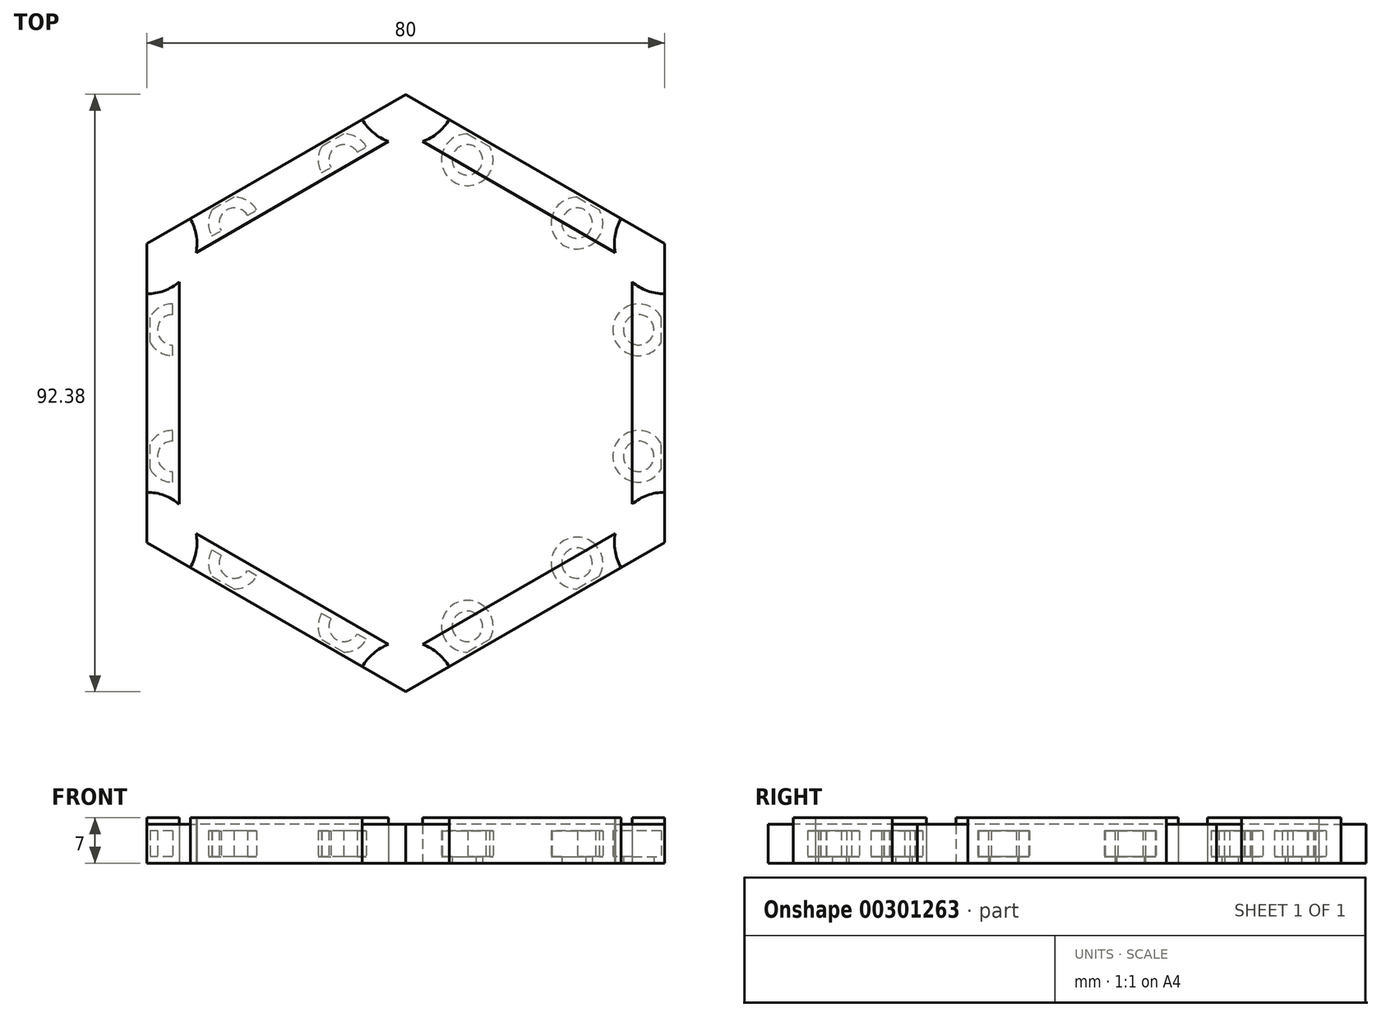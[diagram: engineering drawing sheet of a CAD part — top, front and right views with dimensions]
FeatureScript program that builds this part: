
annotation { "Feature Type Name" : "Feature", "Feature Type Description" : "" }
export const myFeature = defineFeature(function(context is Context, id is Id, definition is map)
    precondition{}
    {
        {
            var Q0;
            Q0=qCreatedBy(makeId("Top.planeOp"),FACE);
            var sketch = newSketch(context, id + "F0", { "sketchPlane" : qUnion([Q0])});
            skCircle(sketch, "E0.cCircle", {"center": v(0, 0) * mm, "radius": 40 * mm, "construction": true});
            skLineSegment(sketch, "E0.0", {"start": v(40, 23.1) * mm, "end": v(40, -23.1) * mm});
            skLineSegment(sketch, "E0.1", {"start": v(40, -23.1) * mm, "end": v(0, -46.19) * mm});
            skLineSegment(sketch, "E0.2", {"start": v(0, -46.19) * mm, "end": v(-40, -23.1) * mm});
            skLineSegment(sketch, "E0.3", {"start": v(-40, -23.1) * mm, "end": v(-40, 23.1) * mm});
            skLineSegment(sketch, "E0.4", {"start": v(-40, 23.1) * mm, "end": v(0, 46.19) * mm});
            skLineSegment(sketch, "E0.5", {"start": v(0, 46.19) * mm, "end": v(40, 23.1) * mm});
            skPoint(sketch, "E0.0.midPoint", {"position": v(40, 0) * mm});
            skCircle(sketch, "E1.cCircle", {"center": v(0, 0) * mm, "radius": 35 * mm, "construction": true});
            skLineSegment(sketch, "E1.0", {"start": v(35, 20.2) * mm, "end": v(35, -20.2) * mm});
            skLineSegment(sketch, "E1.1", {"start": v(35, -20.2) * mm, "end": v(0, -40.41) * mm});
            skLineSegment(sketch, "E1.2", {"start": v(0, -40.41) * mm, "end": v(-35, -20.2) * mm});
            skLineSegment(sketch, "E1.3", {"start": v(-35, -20.2) * mm, "end": v(-35, 20.2) * mm});
            skLineSegment(sketch, "E1.4", {"start": v(-35, 20.2) * mm, "end": v(0, 40.41) * mm});
            skLineSegment(sketch, "E1.5", {"start": v(0, 40.41) * mm, "end": v(35, 20.2) * mm});
            skPoint(sketch, "E1.0.midPoint", {"position": v(35, 0) * mm});
            skArc(sketch, "E2", {"start": v(-40, 15.34) * mm, "mid": v(-33.29, 19.22) * mm, "end": v(-33.29, 26.97) * mm});
            skLineSegment(sketch, "E3", {"start": v(-40, 0) * mm, "end": v(40, 0) * mm, "construction": true});
            skLineSegment(sketch, "E4", {"start": v(-20, -34.64) * mm, "end": v(20, 34.64) * mm, "construction": true});
            skLineSegment(sketch, "E5", {"start": v(-20, 34.64) * mm, "end": v(20, -34.64) * mm, "construction": true});
            skArc(sketch, "E6.MirrorCS", {"start": v(-40, -15.34) * mm, "mid": v(-33.29, -19.22) * mm, "end": v(-33.29, -26.97) * mm});
            skArc(sketch, "E7.MirrorCS", {"start": v(6.71, -42.31) * mm, "mid": v(0, -38.44) * mm, "end": v(-6.71, -42.31) * mm});
            skArc(sketch, "E8.MirrorCS", {"start": v(33.29, -26.97) * mm, "mid": v(33.29, -19.22) * mm, "end": v(40, -15.34) * mm});
            skArc(sketch, "E9.MirrorCS", {"start": v(33.29, 26.97) * mm, "mid": v(33.29, 19.22) * mm, "end": v(40, 15.34) * mm});
            skArc(sketch, "E10.MirrorCS", {"start": v(6.71, 42.31) * mm, "mid": v(0, 38.44) * mm, "end": v(-6.71, 42.31) * mm});
            skSolve(sketch);
        }
        {
            var Q0;
            {var subQ5=sQuery(id+"F0.wireOp",EDGE,"E0.2");var subQ8=sQuery(id+"F0.wireOp",EDGE,"E0.3");var subQ9=makeQuery(id+"F0.imprint","INTERSECT",VERTEX,{"derivedFrom":[subQ5,subQ8]});Q0=makeQuery(id+"F0.imprint","IMPRINT",FACE,{"disambiguationData":[TD([[makeQuery(id+"F0.imprint","IMPRINT",EDGE,{"disambiguationData":[TD([[subQ9,1.0]])],"derivedFrom":subQ5}),-1.0]])]});}
            var Q1;
            {var subQ6=sQuery(id+"F0.wireOp",EDGE,"E0.2");var subQ7=sQuery(id+"F0.wireOp",EDGE,"E0.1");var subQ8=makeQuery(id+"F0.imprint","INTERSECT",VERTEX,{"derivedFrom":[subQ7,subQ6]});Q1=makeQuery(id+"F0.imprint","IMPRINT",FACE,{"disambiguationData":[TD([[makeQuery(id+"F0.imprint","IMPRINT",EDGE,{"disambiguationData":[TD([[subQ8,1.0]])],"derivedFrom":subQ7}),-1.0]])]});}
            var Q2;
            {var subQ6=sQuery(id+"F0.wireOp",EDGE,"E0.1");var subQ7=sQuery(id+"F0.wireOp",EDGE,"E0.0");var subQ8=makeQuery(id+"F0.imprint","INTERSECT",VERTEX,{"derivedFrom":[subQ7,subQ6]});Q2=makeQuery(id+"F0.imprint","IMPRINT",FACE,{"disambiguationData":[TD([[makeQuery(id+"F0.imprint","IMPRINT",EDGE,{"disambiguationData":[TD([[subQ8,1.0]])],"derivedFrom":subQ7}),-1.0]])]});}
            var Q3;
            {var subQ5=sQuery(id+"F0.wireOp",EDGE,"E0.5");var subQ6=sQuery(id+"F0.wireOp",EDGE,"E0.0");var subQ7=makeQuery(id+"F0.imprint","INTERSECT",VERTEX,{"derivedFrom":[subQ6,subQ5]});Q3=makeQuery(id+"F0.imprint","IMPRINT",FACE,{"disambiguationData":[TD([[makeQuery(id+"F0.imprint","IMPRINT",EDGE,{"disambiguationData":[TD([[subQ7,-1.0]])],"derivedFrom":subQ6}),-1.0]])]});}
            var Q4;
            {var subQ5=sQuery(id+"F0.wireOp",EDGE,"E0.4");var subQ8=sQuery(id+"F0.wireOp",EDGE,"E0.5");var subQ9=makeQuery(id+"F0.imprint","INTERSECT",VERTEX,{"derivedFrom":[subQ5,subQ8]});Q4=makeQuery(id+"F0.imprint","IMPRINT",FACE,{"disambiguationData":[TD([[makeQuery(id+"F0.imprint","IMPRINT",EDGE,{"disambiguationData":[TD([[subQ9,1.0]])],"derivedFrom":subQ5}),-1.0]])]});}
            var Q5;
            {var subQ5=sQuery(id+"F0.wireOp",EDGE,"E0.3");var subQ8=sQuery(id+"F0.wireOp",EDGE,"E0.4");var subQ9=makeQuery(id+"F0.imprint","INTERSECT",VERTEX,{"derivedFrom":[subQ5,subQ8]});Q5=makeQuery(id+"F0.imprint","IMPRINT",FACE,{"disambiguationData":[TD([[makeQuery(id+"F0.imprint","IMPRINT",EDGE,{"disambiguationData":[TD([[subQ9,1.0]])],"derivedFrom":subQ5}),-1.0]])]});}
            var Q6;
            {var subQ0=sQuery(id+"F0.wireOp",EDGE,"E1.4");var subQ1=sQuery(id+"F0.wireOp",EDGE,"E1.3");var subQ2=makeQuery(id+"F0.imprint","INTERSECT",VERTEX,{"derivedFrom":[subQ1,subQ0]});Q6=makeQuery(id+"F0.imprint","IMPRINT",FACE,{"disambiguationData":[TD([[makeQuery(id+"F0.imprint","IMPRINT",EDGE,{"disambiguationData":[TD([[subQ2,1.0]])],"derivedFrom":subQ1}),-1.0]])]});}
            var Q7;
            {var subQ0=sQuery(id+"F0.wireOp",EDGE,"E1.5");var subQ1=sQuery(id+"F0.wireOp",EDGE,"E1.4");var subQ2=makeQuery(id+"F0.imprint","INTERSECT",VERTEX,{"derivedFrom":[subQ1,subQ0]});Q7=makeQuery(id+"F0.imprint","IMPRINT",FACE,{"disambiguationData":[TD([[makeQuery(id+"F0.imprint","IMPRINT",EDGE,{"disambiguationData":[TD([[subQ2,1.0]])],"derivedFrom":subQ1}),-1.0]])]});}
            var Q8;
            {var subQ0=sQuery(id+"F0.wireOp",EDGE,"E1.3");var subQ1=sQuery(id+"F0.wireOp",EDGE,"E1.2");var subQ2=makeQuery(id+"F0.imprint","INTERSECT",VERTEX,{"derivedFrom":[subQ1,subQ0]});Q8=makeQuery(id+"F0.imprint","IMPRINT",FACE,{"disambiguationData":[TD([[makeQuery(id+"F0.imprint","IMPRINT",EDGE,{"disambiguationData":[TD([[subQ2,1.0]])],"derivedFrom":subQ1}),-1.0]])]});}
            var Q9;
            {var subQ0=sQuery(id+"F0.wireOp",EDGE,"E1.2");var subQ1=sQuery(id+"F0.wireOp",EDGE,"E1.1");var subQ2=makeQuery(id+"F0.imprint","INTERSECT",VERTEX,{"derivedFrom":[subQ1,subQ0]});Q9=makeQuery(id+"F0.imprint","IMPRINT",FACE,{"disambiguationData":[TD([[makeQuery(id+"F0.imprint","IMPRINT",EDGE,{"disambiguationData":[TD([[subQ2,1.0]])],"derivedFrom":subQ1}),-1.0]])]});}
            var Q10;
            {var subQ0=sQuery(id+"F0.wireOp",EDGE,"E1.1");var subQ1=sQuery(id+"F0.wireOp",EDGE,"E1.0");var subQ2=makeQuery(id+"F0.imprint","INTERSECT",VERTEX,{"derivedFrom":[subQ1,subQ0]});Q10=makeQuery(id+"F0.imprint","IMPRINT",FACE,{"disambiguationData":[TD([[makeQuery(id+"F0.imprint","IMPRINT",EDGE,{"disambiguationData":[TD([[subQ2,1.0]])],"derivedFrom":subQ1}),-1.0]])]});}
            var Q11;
            {var subQ0=sQuery(id+"F0.wireOp",EDGE,"E1.5");var subQ1=sQuery(id+"F0.wireOp",EDGE,"E1.0");var subQ2=makeQuery(id+"F0.imprint","INTERSECT",VERTEX,{"derivedFrom":[subQ1,subQ0]});Q11=makeQuery(id+"F0.imprint","IMPRINT",FACE,{"disambiguationData":[TD([[makeQuery(id+"F0.imprint","IMPRINT",EDGE,{"disambiguationData":[TD([[subQ2,-1.0]])],"derivedFrom":subQ1}),-1.0]])]});}
            var Q12;
            {var subQ1=sQuery(id+"F0.wireOp",EDGE,"E1.0");var subQ20=sQuery(id+"F0.wireOp",EDGE,"E9.MirrorCS");var subQ23=makeQuery(id+"F0.imprint","INTERSECT",VERTEX,{"derivedFrom":[subQ1,subQ20]});Q12=makeQuery(id+"F0.imprint","IMPRINT",FACE,{"disambiguationData":[TD([[makeQuery(id+"F0.imprint","IMPRINT",EDGE,{"disambiguationData":[TD([[subQ23,-1.0]])],"derivedFrom":subQ1}),-1.0]])]});}
            extrude(context, id + "F1", {"entities" : qUnion([Q0, Q1, Q2, Q3, Q4, Q5, Q6, Q7, Q8, Q9, Q10, Q11, Q12]), "depth" : 6 * mm});
        }
        {
            var Q0;
            {var subQ0=sQuery(id+"F0.wireOp",EDGE,"EV8oDvB6-CE55-jG9r-hjDD-bTfNBknIpFl7");var subQ1=sQuery(id+"F0.wireOp",EDGE,"E0.3");var subQ2=makeQuery(id+"F0.imprint","INTERSECT",VERTEX,{"derivedFrom":[subQ1,subQ0]});Q0=makeQuery(id+"F0.imprint","IMPRINT",FACE,{"disambiguationData":[TD([[makeQuery(id+"F0.imprint","IMPRINT",EDGE,{"disambiguationData":[TD([[subQ2,-1.0]])],"derivedFrom":subQ1}),-1.0]])]});}
            var Q1;
            {var subQ0=sQuery(id+"F0.wireOp",EDGE,"EV8oDvB6-CE55-jG9r-hjDD-bTfNBknIpFl7");var subQ1=sQuery(id+"F0.wireOp",EDGE,"E0.2");var subQ2=makeQuery(id+"F0.imprint","INTERSECT",VERTEX,{"derivedFrom":[subQ1,subQ0]});Q1=makeQuery(id+"F0.imprint","IMPRINT",FACE,{"disambiguationData":[TD([[makeQuery(id+"F0.imprint","IMPRINT",EDGE,{"disambiguationData":[TD([[subQ2,1.0]])],"derivedFrom":subQ1}),-1.0]])]});}
            var Q2;
            {var subQ0=sQuery(id+"F0.wireOp",EDGE,"egI94seK-npkn-q5fv-bbl5-Jg6Q8FrYPwKS");var subQ1=sQuery(id+"F0.wireOp",EDGE,"E0.1");var subQ2=makeQuery(id+"F0.imprint","INTERSECT",VERTEX,{"derivedFrom":[subQ1,subQ0]});Q2=makeQuery(id+"F0.imprint","IMPRINT",FACE,{"disambiguationData":[TD([[makeQuery(id+"F0.imprint","IMPRINT",EDGE,{"disambiguationData":[TD([[subQ2,-1.0]])],"derivedFrom":subQ1}),-1.0]])]});}
            var Q3;
            {var subQ0=sQuery(id+"F0.wireOp",EDGE,"KafPzJvw-o0QC-8g3e-lsn4-mWSbOJhtwsbd");var subQ1=sQuery(id+"F0.wireOp",EDGE,"E0.0");var subQ2=makeQuery(id+"F0.imprint","INTERSECT",VERTEX,{"derivedFrom":[subQ1,subQ0]});Q3=makeQuery(id+"F0.imprint","IMPRINT",FACE,{"disambiguationData":[TD([[makeQuery(id+"F0.imprint","IMPRINT",EDGE,{"disambiguationData":[TD([[subQ2,-1.0]])],"derivedFrom":subQ1}),-1.0]])]});}
            var Q4;
            {var subQ0=sQuery(id+"F0.wireOp",EDGE,"k6S9yhyR-1Vpb-fnxe-gLg6-2WvRY6sDJVSI");var subQ1=sQuery(id+"F0.wireOp",EDGE,"E0.5");var subQ2=makeQuery(id+"F0.imprint","INTERSECT",VERTEX,{"derivedFrom":[subQ1,subQ0]});Q4=makeQuery(id+"F0.imprint","IMPRINT",FACE,{"disambiguationData":[TD([[makeQuery(id+"F0.imprint","IMPRINT",EDGE,{"disambiguationData":[TD([[subQ2,-1.0]])],"derivedFrom":subQ1}),-1.0]])]});}
            var Q5;
            {var subQ0=sQuery(id+"F0.wireOp",EDGE,"4XjSm9CI-rTLO-w5t8-ErOd-Ri5MCnTNQxzr");var subQ1=sQuery(id+"F0.wireOp",EDGE,"E0.4");var subQ2=makeQuery(id+"F0.imprint","INTERSECT",VERTEX,{"derivedFrom":[subQ1,subQ0]});Q5=makeQuery(id+"F0.imprint","IMPRINT",FACE,{"disambiguationData":[TD([[makeQuery(id+"F0.imprint","IMPRINT",EDGE,{"disambiguationData":[TD([[subQ2,-1.0]])],"derivedFrom":subQ1}),-1.0]])]});}
            extrude(context, id + "F2", {"entities" : qUnion([Q0, Q1, Q2, Q3, Q4, Q5]), "depth" : 7 * mm});
        }
        {
            var Q0;
            {var subQ0=sQuery(id+"F0.wireOp",EDGE,"KafPzJvw-o0QC-8g3e-lsn4-mWSbOJhtwsbd");var subQ1=sQuery(id+"F0.wireOp",EDGE,"E1.0");var subQ2=makeQuery(id+"F0.imprint","INTERSECT",VERTEX,{"derivedFrom":[subQ1,subQ0]});Q0=makeQuery(id+"F0.imprint","IMPRINT",FACE,{"disambiguationData":[TD([[makeQuery(id+"F0.imprint","IMPRINT",EDGE,{"disambiguationData":[TD([[subQ2,-1.0]])],"derivedFrom":subQ1}),-1.0]])]});}
            var sketch = newSketch(context, id + "F3", { "sketchPlane" : qUnion([Q0])});
            skCircle(sketch, "E11.cCircle", {"center": v(0, 0) * mm, "radius": 36 * mm, "construction": true});
            skLineSegment(sketch, "E11.0", {"start": v(36, 20.78) * mm, "end": v(36, -20.78) * mm});
            skLineSegment(sketch, "E11.1", {"start": v(36, -20.78) * mm, "end": v(0, -41.57) * mm});
            skLineSegment(sketch, "E11.2", {"start": v(0, -41.57) * mm, "end": v(-36, -20.78) * mm});
            skLineSegment(sketch, "E11.3", {"start": v(-36, -20.78) * mm, "end": v(-36, 20.78) * mm});
            skLineSegment(sketch, "E11.4", {"start": v(-36, 20.78) * mm, "end": v(0, 41.57) * mm});
            skLineSegment(sketch, "E11.5", {"start": v(0, 41.57) * mm, "end": v(36, 20.78) * mm});
            skPoint(sketch, "E11.0.midPoint", {"position": v(36, 0) * mm});
            skLineSegment(sketch, "E12.MirrorCS", {"start": v(-36, -20.78) * mm, "end": v(-26.47, -26.28) * mm});
            skLineSegment(sketch, "E13.MirrorCS", {"start": v(-36, 20.78) * mm, "end": v(-36, -20.78) * mm});
            skLineSegment(sketch, "E14.MirrorCS", {"start": v(0, 41.57) * mm, "end": v(-36, 20.78) * mm});
            skLineSegment(sketch, "E15", {"start": v(-26.47, -26.28) * mm, "end": v(-9.53, -36.07) * mm});
            skLineSegment(sketch, "E16", {"start": v(-9.53, -36.07) * mm, "end": v(0, -41.57) * mm});
            skCircle(sketch, "E17", {"center": v(-26.47, -26.28) * mm, "radius": 2.35 * mm});
            skCircle(sketch, "E18", {"center": v(-9.53, -36.07) * mm, "radius": 2.35 * mm});
            skLineSegment(sketch, "E19", {"start": v(-36, -20.78) * mm, "end": v(36, 20.78) * mm, "construction": true});
            skLineSegment(sketch, "E20", {"start": v(-36, 20.78) * mm, "end": v(36, -20.78) * mm, "construction": true});
            skLineSegment(sketch, "E21", {"start": v(0, -41.57) * mm, "end": v(0, 41.57) * mm, "construction": true});
            skCircle(sketch, "E22.MirrorC", {"center": v(-36, -9.78) * mm, "radius": 2.35 * mm});
            skCircle(sketch, "E23.MirrorC", {"center": v(-36, 9.78) * mm, "radius": 2.35 * mm});
            skCircle(sketch, "E24.MirrorC", {"center": v(-26.47, 26.28) * mm, "radius": 2.35 * mm});
            skCircle(sketch, "E25.MirrorC", {"center": v(-9.53, 36.07) * mm, "radius": 2.35 * mm});
            skCircle(sketch, "E26.MirrorC", {"center": v(9.53, 36.07) * mm, "radius": 2.35 * mm});
            skCircle(sketch, "E27.MirrorC", {"center": v(26.47, 26.28) * mm, "radius": 2.35 * mm});
            skCircle(sketch, "E28.MirrorC", {"center": v(36, 9.78) * mm, "radius": 2.35 * mm});
            skCircle(sketch, "E29.MirrorC", {"center": v(36, -9.78) * mm, "radius": 2.35 * mm});
            skCircle(sketch, "E30.MirrorC", {"center": v(26.47, -26.28) * mm, "radius": 2.35 * mm});
            skCircle(sketch, "E31.MirrorC", {"center": v(9.53, -36.07) * mm, "radius": 2.35 * mm});
            skArc(sketch, "E32", {"start": v(-26.55, -30.28) * mm, "mid": v(-24.47, -22.82) * mm, "end": v(-29.9, -28.35) * mm});
            skLineSegment(sketch, "E33", {"start": v(-29.9, -28.35) * mm, "end": v(-26.55, -30.28) * mm});
            skArc(sketch, "E34", {"start": v(-12.95, -38.13) * mm, "mid": v(-7.53, -32.6) * mm, "end": v(-9.6, -40.07) * mm});
            skLineSegment(sketch, "E35", {"start": v(-12.95, -38.13) * mm, "end": v(-9.6, -40.07) * mm});
            skArc(sketch, "E36.MirrorCS", {"start": v(-39.5, -7.85) * mm, "mid": v(-32, -9.78) * mm, "end": v(-39.5, -11.72) * mm});
            skLineSegment(sketch, "E37.MirrorCS", {"start": v(-39.5, -11.72) * mm, "end": v(-39.5, -7.85) * mm});
            skArc(sketch, "E38.MirrorCS", {"start": v(-39.5, 7.85) * mm, "mid": v(-32, 9.78) * mm, "end": v(-39.5, 11.72) * mm});
            skLineSegment(sketch, "E39.MirrorCS", {"start": v(-39.5, 7.85) * mm, "end": v(-39.5, 11.72) * mm});
            skArc(sketch, "E40.MirrorCS", {"start": v(-12.95, 38.13) * mm, "mid": v(-7.53, 32.6) * mm, "end": v(-9.6, 40.07) * mm});
            skLineSegment(sketch, "E41.MirrorCS", {"start": v(-9.6, 40.07) * mm, "end": v(-12.95, 38.13) * mm});
            skArc(sketch, "E42.MirrorCS", {"start": v(-26.55, 30.28) * mm, "mid": v(-24.47, 22.82) * mm, "end": v(-29.9, 28.35) * mm});
            skLineSegment(sketch, "E43.MirrorCS", {"start": v(-26.55, 30.28) * mm, "end": v(-29.9, 28.35) * mm});
            skArc(sketch, "E44.MirrorCS", {"start": v(12.95, 38.13) * mm, "mid": v(7.53, 32.6) * mm, "end": v(9.6, 40.07) * mm});
            skLineSegment(sketch, "E45.MirrorCS", {"start": v(9.6, 40.07) * mm, "end": v(12.95, 38.13) * mm});
            skLineSegment(sketch, "E46.MirrorCS", {"start": v(26.55, 30.28) * mm, "end": v(29.9, 28.35) * mm});
            skArc(sketch, "E47.MirrorCS", {"start": v(26.55, 30.28) * mm, "mid": v(24.47, 22.82) * mm, "end": v(29.9, 28.35) * mm});
            skArc(sketch, "E48.MirrorCS", {"start": v(39.5, 7.85) * mm, "mid": v(32, 9.78) * mm, "end": v(39.5, 11.72) * mm});
            skLineSegment(sketch, "E49.MirrorCS", {"start": v(39.5, 7.85) * mm, "end": v(39.5, 11.72) * mm});
            skArc(sketch, "E50.MirrorCS", {"start": v(39.5, -7.85) * mm, "mid": v(32, -9.78) * mm, "end": v(39.5, -11.72) * mm});
            skLineSegment(sketch, "E51.MirrorCS", {"start": v(39.5, -11.72) * mm, "end": v(39.5, -7.85) * mm});
            skArc(sketch, "E52.MirrorCS", {"start": v(26.55, -30.28) * mm, "mid": v(24.47, -22.82) * mm, "end": v(29.9, -28.35) * mm});
            skLineSegment(sketch, "E53.MirrorCS", {"start": v(29.9, -28.35) * mm, "end": v(26.55, -30.28) * mm});
            skArc(sketch, "E54.MirrorCS", {"start": v(12.95, -38.13) * mm, "mid": v(7.53, -32.6) * mm, "end": v(9.6, -40.07) * mm});
            skLineSegment(sketch, "E55.MirrorCS", {"start": v(12.95, -38.13) * mm, "end": v(9.6, -40.07) * mm});
            skSolve(sketch);
        }
        {
            var Q0;
            {var subQ0=sQuery(id+"F3.wireOp",EDGE,"E22.MirrorC");var subQ1=sQuery(id+"F3.wireOp",EDGE,"E13.MirrorCS");var subQ2=makeQuery(id+"F3.imprint","INTERSECT",VERTEX,{"disambiguationData":[OD(0.0)],"derivedFrom":[subQ1,subQ0]});Q0=makeQuery(id+"F3.imprint","IMPRINT",FACE,{"disambiguationData":[TD([[makeQuery(id+"F3.imprint","IMPRINT",EDGE,{"disambiguationData":[TD([[subQ2,-1.0]])],"derivedFrom":subQ1}),1.0]])]});}
            var Q1;
            {var subQ0=sQuery(id+"F3.wireOp",EDGE,"E22.MirrorC");var subQ1=sQuery(id+"F3.wireOp",EDGE,"E13.MirrorCS");var subQ2=makeQuery(id+"F3.imprint","INTERSECT",VERTEX,{"disambiguationData":[OD(0.0)],"derivedFrom":[subQ1,subQ0]});Q1=makeQuery(id+"F3.imprint","IMPRINT",FACE,{"disambiguationData":[TD([[makeQuery(id+"F3.imprint","IMPRINT",EDGE,{"disambiguationData":[TD([[subQ2,-1.0]])],"derivedFrom":subQ1}),-1.0]])]});}
            var Q2;
            {var subQ0=sQuery(id+"F3.wireOp",EDGE,"E23.MirrorC");var subQ1=sQuery(id+"F3.wireOp",EDGE,"E13.MirrorCS");var subQ2=makeQuery(id+"F3.imprint","INTERSECT",VERTEX,{"disambiguationData":[OD(0.0)],"derivedFrom":[subQ1,subQ0]});Q2=makeQuery(id+"F3.imprint","IMPRINT",FACE,{"disambiguationData":[TD([[makeQuery(id+"F3.imprint","IMPRINT",EDGE,{"disambiguationData":[TD([[subQ2,-1.0]])],"derivedFrom":subQ1}),-1.0]])]});}
            var Q3;
            {var subQ0=sQuery(id+"F3.wireOp",EDGE,"E23.MirrorC");var subQ1=sQuery(id+"F3.wireOp",EDGE,"E13.MirrorCS");var subQ2=makeQuery(id+"F3.imprint","INTERSECT",VERTEX,{"disambiguationData":[OD(0.0)],"derivedFrom":[subQ1,subQ0]});Q3=makeQuery(id+"F3.imprint","IMPRINT",FACE,{"disambiguationData":[TD([[makeQuery(id+"F3.imprint","IMPRINT",EDGE,{"disambiguationData":[TD([[subQ2,-1.0]])],"derivedFrom":subQ1}),1.0]])]});}
            var Q4;
            {var subQ0=sQuery(id+"F3.wireOp",EDGE,"E24.MirrorC");var subQ1=sQuery(id+"F3.wireOp",EDGE,"E14.MirrorCS");var subQ2=makeQuery(id+"F3.imprint","INTERSECT",VERTEX,{"disambiguationData":[OD(0.0)],"derivedFrom":[subQ1,subQ0]});Q4=makeQuery(id+"F3.imprint","IMPRINT",FACE,{"disambiguationData":[TD([[makeQuery(id+"F3.imprint","IMPRINT",EDGE,{"disambiguationData":[TD([[subQ2,-1.0]])],"derivedFrom":subQ1}),-1.0]])]});}
            var Q5;
            {var subQ0=sQuery(id+"F3.wireOp",EDGE,"E24.MirrorC");var subQ1=sQuery(id+"F3.wireOp",EDGE,"E14.MirrorCS");var subQ2=makeQuery(id+"F3.imprint","INTERSECT",VERTEX,{"disambiguationData":[OD(0.0)],"derivedFrom":[subQ1,subQ0]});Q5=makeQuery(id+"F3.imprint","IMPRINT",FACE,{"disambiguationData":[TD([[makeQuery(id+"F3.imprint","IMPRINT",EDGE,{"disambiguationData":[TD([[subQ2,-1.0]])],"derivedFrom":subQ1}),1.0]])]});}
            var Q6;
            {var subQ0=sQuery(id+"F3.wireOp",EDGE,"E25.MirrorC");var subQ1=sQuery(id+"F3.wireOp",EDGE,"E14.MirrorCS");var subQ2=makeQuery(id+"F3.imprint","INTERSECT",VERTEX,{"disambiguationData":[OD(0.0)],"derivedFrom":[subQ1,subQ0]});Q6=makeQuery(id+"F3.imprint","IMPRINT",FACE,{"disambiguationData":[TD([[makeQuery(id+"F3.imprint","IMPRINT",EDGE,{"disambiguationData":[TD([[subQ2,-1.0]])],"derivedFrom":subQ1}),-1.0]])]});}
            var Q7;
            {var subQ0=sQuery(id+"F3.wireOp",EDGE,"E25.MirrorC");var subQ1=sQuery(id+"F3.wireOp",EDGE,"E14.MirrorCS");var subQ2=makeQuery(id+"F3.imprint","INTERSECT",VERTEX,{"disambiguationData":[OD(0.0)],"derivedFrom":[subQ1,subQ0]});Q7=makeQuery(id+"F3.imprint","IMPRINT",FACE,{"disambiguationData":[TD([[makeQuery(id+"F3.imprint","IMPRINT",EDGE,{"disambiguationData":[TD([[subQ2,-1.0]])],"derivedFrom":subQ1}),1.0]])]});}
            var Q8;
            {var subQ0=sQuery(id+"F3.wireOp",EDGE,"E26.MirrorC");var subQ1=sQuery(id+"F3.wireOp",EDGE,"E11.5");var subQ2=makeQuery(id+"F3.imprint","INTERSECT",VERTEX,{"disambiguationData":[OD(0.0)],"derivedFrom":[subQ1,subQ0]});Q8=makeQuery(id+"F3.imprint","IMPRINT",FACE,{"disambiguationData":[TD([[makeQuery(id+"F3.imprint","IMPRINT",EDGE,{"disambiguationData":[TD([[subQ2,-1.0]])],"derivedFrom":subQ1}),-1.0]])]});}
            var Q9;
            {var subQ0=sQuery(id+"F3.wireOp",EDGE,"E26.MirrorC");var subQ1=sQuery(id+"F3.wireOp",EDGE,"E11.5");var subQ2=makeQuery(id+"F3.imprint","INTERSECT",VERTEX,{"disambiguationData":[OD(0.0)],"derivedFrom":[subQ1,subQ0]});Q9=makeQuery(id+"F3.imprint","IMPRINT",FACE,{"disambiguationData":[TD([[makeQuery(id+"F3.imprint","IMPRINT",EDGE,{"disambiguationData":[TD([[subQ2,-1.0]])],"derivedFrom":subQ1}),1.0]])]});}
            var Q10;
            {var subQ0=sQuery(id+"F3.wireOp",EDGE,"E27.MirrorC");var subQ1=sQuery(id+"F3.wireOp",EDGE,"E11.5");var subQ2=makeQuery(id+"F3.imprint","INTERSECT",VERTEX,{"disambiguationData":[OD(0.0)],"derivedFrom":[subQ1,subQ0]});Q10=makeQuery(id+"F3.imprint","IMPRINT",FACE,{"disambiguationData":[TD([[makeQuery(id+"F3.imprint","IMPRINT",EDGE,{"disambiguationData":[TD([[subQ2,-1.0]])],"derivedFrom":subQ1}),-1.0]])]});}
            var Q11;
            {var subQ0=sQuery(id+"F3.wireOp",EDGE,"E27.MirrorC");var subQ1=sQuery(id+"F3.wireOp",EDGE,"E11.5");var subQ2=makeQuery(id+"F3.imprint","INTERSECT",VERTEX,{"disambiguationData":[OD(0.0)],"derivedFrom":[subQ1,subQ0]});Q11=makeQuery(id+"F3.imprint","IMPRINT",FACE,{"disambiguationData":[TD([[makeQuery(id+"F3.imprint","IMPRINT",EDGE,{"disambiguationData":[TD([[subQ2,-1.0]])],"derivedFrom":subQ1}),1.0]])]});}
            var Q12;
            {var subQ0=sQuery(id+"F3.wireOp",EDGE,"E28.MirrorC");var subQ1=sQuery(id+"F3.wireOp",EDGE,"E11.0");var subQ2=makeQuery(id+"F3.imprint","INTERSECT",VERTEX,{"disambiguationData":[OD(0.0)],"derivedFrom":[subQ1,subQ0]});Q12=makeQuery(id+"F3.imprint","IMPRINT",FACE,{"disambiguationData":[TD([[makeQuery(id+"F3.imprint","IMPRINT",EDGE,{"disambiguationData":[TD([[subQ2,-1.0]])],"derivedFrom":subQ1}),-1.0]])]});}
            var Q13;
            {var subQ0=sQuery(id+"F3.wireOp",EDGE,"E28.MirrorC");var subQ1=sQuery(id+"F3.wireOp",EDGE,"E11.0");var subQ2=makeQuery(id+"F3.imprint","INTERSECT",VERTEX,{"disambiguationData":[OD(0.0)],"derivedFrom":[subQ1,subQ0]});Q13=makeQuery(id+"F3.imprint","IMPRINT",FACE,{"disambiguationData":[TD([[makeQuery(id+"F3.imprint","IMPRINT",EDGE,{"disambiguationData":[TD([[subQ2,-1.0]])],"derivedFrom":subQ1}),1.0]])]});}
            var Q14;
            {var subQ0=sQuery(id+"F3.wireOp",EDGE,"E29.MirrorC");var subQ1=sQuery(id+"F3.wireOp",EDGE,"E11.0");var subQ2=makeQuery(id+"F3.imprint","INTERSECT",VERTEX,{"disambiguationData":[OD(0.0)],"derivedFrom":[subQ1,subQ0]});Q14=makeQuery(id+"F3.imprint","IMPRINT",FACE,{"disambiguationData":[TD([[makeQuery(id+"F3.imprint","IMPRINT",EDGE,{"disambiguationData":[TD([[subQ2,-1.0]])],"derivedFrom":subQ1}),-1.0]])]});}
            var Q15;
            {var subQ0=sQuery(id+"F3.wireOp",EDGE,"E29.MirrorC");var subQ1=sQuery(id+"F3.wireOp",EDGE,"E11.0");var subQ2=makeQuery(id+"F3.imprint","INTERSECT",VERTEX,{"disambiguationData":[OD(0.0)],"derivedFrom":[subQ1,subQ0]});Q15=makeQuery(id+"F3.imprint","IMPRINT",FACE,{"disambiguationData":[TD([[makeQuery(id+"F3.imprint","IMPRINT",EDGE,{"disambiguationData":[TD([[subQ2,-1.0]])],"derivedFrom":subQ1}),1.0]])]});}
            var Q16;
            {var subQ0=sQuery(id+"F3.wireOp",EDGE,"E30.MirrorC");var subQ1=sQuery(id+"F3.wireOp",EDGE,"E11.1");var subQ2=makeQuery(id+"F3.imprint","INTERSECT",VERTEX,{"disambiguationData":[OD(0.0)],"derivedFrom":[subQ1,subQ0]});Q16=makeQuery(id+"F3.imprint","IMPRINT",FACE,{"disambiguationData":[TD([[makeQuery(id+"F3.imprint","IMPRINT",EDGE,{"disambiguationData":[TD([[subQ2,-1.0]])],"derivedFrom":subQ1}),1.0]])]});}
            var Q17;
            {var subQ0=sQuery(id+"F3.wireOp",EDGE,"E30.MirrorC");var subQ1=sQuery(id+"F3.wireOp",EDGE,"E11.1");var subQ2=makeQuery(id+"F3.imprint","INTERSECT",VERTEX,{"disambiguationData":[OD(0.0)],"derivedFrom":[subQ1,subQ0]});Q17=makeQuery(id+"F3.imprint","IMPRINT",FACE,{"disambiguationData":[TD([[makeQuery(id+"F3.imprint","IMPRINT",EDGE,{"disambiguationData":[TD([[subQ2,-1.0]])],"derivedFrom":subQ1}),-1.0]])]});}
            var Q18;
            {var subQ0=sQuery(id+"F3.wireOp",EDGE,"E31.MirrorC");var subQ1=sQuery(id+"F3.wireOp",EDGE,"E11.1");var subQ2=makeQuery(id+"F3.imprint","INTERSECT",VERTEX,{"disambiguationData":[OD(0.0)],"derivedFrom":[subQ1,subQ0]});Q18=makeQuery(id+"F3.imprint","IMPRINT",FACE,{"disambiguationData":[TD([[makeQuery(id+"F3.imprint","IMPRINT",EDGE,{"disambiguationData":[TD([[subQ2,-1.0]])],"derivedFrom":subQ1}),1.0]])]});}
            var Q19;
            {var subQ0=sQuery(id+"F3.wireOp",EDGE,"E31.MirrorC");var subQ1=sQuery(id+"F3.wireOp",EDGE,"E11.1");var subQ2=makeQuery(id+"F3.imprint","INTERSECT",VERTEX,{"disambiguationData":[OD(0.0)],"derivedFrom":[subQ1,subQ0]});Q19=makeQuery(id+"F3.imprint","IMPRINT",FACE,{"disambiguationData":[TD([[makeQuery(id+"F3.imprint","IMPRINT",EDGE,{"disambiguationData":[TD([[subQ2,-1.0]])],"derivedFrom":subQ1}),-1.0]])]});}
            var Q20;
            {var subQ0=sQuery(id+"F3.wireOp",EDGE,"E16");var subQ1=sQuery(id+"F3.wireOp",EDGE,"E15");var subQ2=makeQuery(id+"F3.imprint","INTERSECT",VERTEX,{"derivedFrom":[subQ1,subQ0]});Q20=makeQuery(id+"F3.imprint","IMPRINT",FACE,{"disambiguationData":[TD([[makeQuery(id+"F3.imprint","IMPRINT",EDGE,{"disambiguationData":[TD([[subQ2,1.0]])],"derivedFrom":subQ1}),-1.0]])]});}
            var Q21;
            {var subQ0=sQuery(id+"F3.wireOp",EDGE,"E16");var subQ1=sQuery(id+"F3.wireOp",EDGE,"E15");var subQ2=makeQuery(id+"F3.imprint","INTERSECT",VERTEX,{"derivedFrom":[subQ1,subQ0]});Q21=makeQuery(id+"F3.imprint","IMPRINT",FACE,{"disambiguationData":[TD([[makeQuery(id+"F3.imprint","IMPRINT",EDGE,{"disambiguationData":[TD([[subQ2,1.0]])],"derivedFrom":subQ1}),1.0]])]});}
            var Q22;
            {var subQ0=sQuery(id+"F3.wireOp",EDGE,"E15");var subQ1=sQuery(id+"F3.wireOp",EDGE,"E12.MirrorCS");var subQ2=makeQuery(id+"F3.imprint","INTERSECT",VERTEX,{"derivedFrom":[subQ1,subQ0]});Q22=makeQuery(id+"F3.imprint","IMPRINT",FACE,{"disambiguationData":[TD([[makeQuery(id+"F3.imprint","IMPRINT",EDGE,{"disambiguationData":[TD([[subQ2,1.0]])],"derivedFrom":subQ1}),-1.0]])]});}
            var Q23;
            {var subQ0=sQuery(id+"F3.wireOp",EDGE,"E15");var subQ1=sQuery(id+"F3.wireOp",EDGE,"E12.MirrorCS");var subQ2=makeQuery(id+"F3.imprint","INTERSECT",VERTEX,{"derivedFrom":[subQ1,subQ0]});Q23=makeQuery(id+"F3.imprint","IMPRINT",FACE,{"disambiguationData":[TD([[makeQuery(id+"F3.imprint","IMPRINT",EDGE,{"disambiguationData":[TD([[subQ2,1.0]])],"derivedFrom":subQ1}),1.0]])]});}
            extrude(context, id + "F4", {"entities" : qUnion([Q0, Q1, Q2, Q3, Q4, Q5, Q6, Q7, Q8, Q9, Q10, Q11, Q12, Q13, Q14, Q15, Q16, Q17, Q18, Q19, Q20, Q21, Q22, Q23]), "operationType" : NewBodyOperationType.REMOVE, "depth" : 5 * mm});
        }
        {
            var Q0;
            {var subQ4=sQuery(id+"F3.wireOp",EDGE,"E37.MirrorCS");Q0=makeQuery(id+"F3.imprint","IMPRINT",FACE,{"disambiguationData":[TD([[makeQuery(id+"F3.imprint","IMPRINT",EDGE,{"derivedFrom":subQ4}),-1.0]])]});}
            var Q1;
            {var subQ0=sQuery(id+"F3.wireOp",EDGE,"E36.MirrorCS");var subQ1=sQuery(id+"F3.wireOp",EDGE,"E13.MirrorCS");var subQ2=makeQuery(id+"F3.imprint","INTERSECT",VERTEX,{"disambiguationData":[OD(0.0)],"derivedFrom":[subQ1,subQ0]});Q1=makeQuery(id+"F3.imprint","IMPRINT",FACE,{"disambiguationData":[TD([[makeQuery(id+"F3.imprint","IMPRINT",EDGE,{"disambiguationData":[TD([[subQ2,-1.0]])],"derivedFrom":subQ1}),1.0]])]});}
            var Q2;
            {var subQ5=sQuery(id+"F3.wireOp",EDGE,"E39.MirrorCS");Q2=makeQuery(id+"F3.imprint","IMPRINT",FACE,{"disambiguationData":[TD([[makeQuery(id+"F3.imprint","IMPRINT",EDGE,{"derivedFrom":subQ5}),-1.0]])]});}
            var Q3;
            {var subQ0=sQuery(id+"F3.wireOp",EDGE,"E38.MirrorCS");var subQ1=sQuery(id+"F3.wireOp",EDGE,"E13.MirrorCS");var subQ2=makeQuery(id+"F3.imprint","INTERSECT",VERTEX,{"disambiguationData":[OD(0.0)],"derivedFrom":[subQ1,subQ0]});Q3=makeQuery(id+"F3.imprint","IMPRINT",FACE,{"disambiguationData":[TD([[makeQuery(id+"F3.imprint","IMPRINT",EDGE,{"disambiguationData":[TD([[subQ2,-1.0]])],"derivedFrom":subQ1}),1.0]])]});}
            var Q4;
            {var subQ6=sQuery(id+"F3.wireOp",EDGE,"E43.MirrorCS");Q4=makeQuery(id+"F3.imprint","IMPRINT",FACE,{"disambiguationData":[TD([[makeQuery(id+"F3.imprint","IMPRINT",EDGE,{"derivedFrom":subQ6}),1.0]])]});}
            var Q5;
            {var subQ0=sQuery(id+"F3.wireOp",EDGE,"E42.MirrorCS");var subQ1=sQuery(id+"F3.wireOp",EDGE,"E14.MirrorCS");var subQ2=makeQuery(id+"F3.imprint","INTERSECT",VERTEX,{"disambiguationData":[OD(0.0)],"derivedFrom":[subQ1,subQ0]});Q5=makeQuery(id+"F3.imprint","IMPRINT",FACE,{"disambiguationData":[TD([[makeQuery(id+"F3.imprint","IMPRINT",EDGE,{"disambiguationData":[TD([[subQ2,-1.0]])],"derivedFrom":subQ1}),1.0]])]});}
            var Q6;
            {var subQ6=sQuery(id+"F3.wireOp",EDGE,"E41.MirrorCS");Q6=makeQuery(id+"F3.imprint","IMPRINT",FACE,{"disambiguationData":[TD([[makeQuery(id+"F3.imprint","IMPRINT",EDGE,{"derivedFrom":subQ6}),1.0]])]});}
            var Q7;
            {var subQ0=sQuery(id+"F3.wireOp",EDGE,"E40.MirrorCS");var subQ1=sQuery(id+"F3.wireOp",EDGE,"E14.MirrorCS");var subQ2=makeQuery(id+"F3.imprint","INTERSECT",VERTEX,{"disambiguationData":[OD(0.0)],"derivedFrom":[subQ1,subQ0]});Q7=makeQuery(id+"F3.imprint","IMPRINT",FACE,{"disambiguationData":[TD([[makeQuery(id+"F3.imprint","IMPRINT",EDGE,{"disambiguationData":[TD([[subQ2,-1.0]])],"derivedFrom":subQ1}),1.0]])]});}
            var Q8;
            {var subQ0=sQuery(id+"F3.wireOp",EDGE,"E44.MirrorCS");var subQ1=sQuery(id+"F3.wireOp",EDGE,"E11.5");var subQ2=makeQuery(id+"F3.imprint","INTERSECT",VERTEX,{"disambiguationData":[OD(0.0)],"derivedFrom":[subQ1,subQ0]});Q8=makeQuery(id+"F3.imprint","IMPRINT",FACE,{"disambiguationData":[TD([[makeQuery(id+"F3.imprint","IMPRINT",EDGE,{"disambiguationData":[TD([[subQ2,-1.0]])],"derivedFrom":subQ1}),-1.0]])]});}
            var Q9;
            {var subQ0=sQuery(id+"F3.wireOp",EDGE,"E45.MirrorCS");Q9=makeQuery(id+"F3.imprint","IMPRINT",FACE,{"disambiguationData":[TD([[makeQuery(id+"F3.imprint","IMPRINT",EDGE,{"derivedFrom":subQ0}),-1.0]])]});}
            var Q10;
            {var subQ0=sQuery(id+"F3.wireOp",EDGE,"E47.MirrorCS");var subQ1=sQuery(id+"F3.wireOp",EDGE,"E11.5");var subQ2=makeQuery(id+"F3.imprint","INTERSECT",VERTEX,{"disambiguationData":[OD(0.0)],"derivedFrom":[subQ1,subQ0]});Q10=makeQuery(id+"F3.imprint","IMPRINT",FACE,{"disambiguationData":[TD([[makeQuery(id+"F3.imprint","IMPRINT",EDGE,{"disambiguationData":[TD([[subQ2,-1.0]])],"derivedFrom":subQ1}),-1.0]])]});}
            var Q11;
            {var subQ0=sQuery(id+"F3.wireOp",EDGE,"E46.MirrorCS");Q11=makeQuery(id+"F3.imprint","IMPRINT",FACE,{"disambiguationData":[TD([[makeQuery(id+"F3.imprint","IMPRINT",EDGE,{"derivedFrom":subQ0}),-1.0]])]});}
            var Q12;
            {var subQ0=sQuery(id+"F3.wireOp",EDGE,"E48.MirrorCS");var subQ1=sQuery(id+"F3.wireOp",EDGE,"E11.0");var subQ2=makeQuery(id+"F3.imprint","INTERSECT",VERTEX,{"disambiguationData":[OD(0.0)],"derivedFrom":[subQ1,subQ0]});Q12=makeQuery(id+"F3.imprint","IMPRINT",FACE,{"disambiguationData":[TD([[makeQuery(id+"F3.imprint","IMPRINT",EDGE,{"disambiguationData":[TD([[subQ2,-1.0]])],"derivedFrom":subQ1}),-1.0]])]});}
            var Q13;
            {var subQ0=sQuery(id+"F3.wireOp",EDGE,"E49.MirrorCS");Q13=makeQuery(id+"F3.imprint","IMPRINT",FACE,{"disambiguationData":[TD([[makeQuery(id+"F3.imprint","IMPRINT",EDGE,{"derivedFrom":subQ0}),1.0]])]});}
            var Q14;
            {var subQ0=sQuery(id+"F3.wireOp",EDGE,"E51.MirrorCS");Q14=makeQuery(id+"F3.imprint","IMPRINT",FACE,{"disambiguationData":[TD([[makeQuery(id+"F3.imprint","IMPRINT",EDGE,{"derivedFrom":subQ0}),1.0]])]});}
            var Q15;
            {var subQ0=sQuery(id+"F3.wireOp",EDGE,"E50.MirrorCS");var subQ1=sQuery(id+"F3.wireOp",EDGE,"E11.0");var subQ2=makeQuery(id+"F3.imprint","INTERSECT",VERTEX,{"disambiguationData":[OD(0.0)],"derivedFrom":[subQ1,subQ0]});Q15=makeQuery(id+"F3.imprint","IMPRINT",FACE,{"disambiguationData":[TD([[makeQuery(id+"F3.imprint","IMPRINT",EDGE,{"disambiguationData":[TD([[subQ2,-1.0]])],"derivedFrom":subQ1}),-1.0]])]});}
            var Q16;
            {var subQ0=sQuery(id+"F3.wireOp",EDGE,"E52.MirrorCS");var subQ1=sQuery(id+"F3.wireOp",EDGE,"E11.1");var subQ2=makeQuery(id+"F3.imprint","INTERSECT",VERTEX,{"disambiguationData":[OD(0.0)],"derivedFrom":[subQ1,subQ0]});Q16=makeQuery(id+"F3.imprint","IMPRINT",FACE,{"disambiguationData":[TD([[makeQuery(id+"F3.imprint","IMPRINT",EDGE,{"disambiguationData":[TD([[subQ2,-1.0]])],"derivedFrom":subQ1}),-1.0]])]});}
            var Q17;
            {var subQ4=sQuery(id+"F3.wireOp",EDGE,"E53.MirrorCS");Q17=makeQuery(id+"F3.imprint","IMPRINT",FACE,{"disambiguationData":[TD([[makeQuery(id+"F3.imprint","IMPRINT",EDGE,{"derivedFrom":subQ4}),-1.0]])]});}
            var Q18;
            {var subQ0=sQuery(id+"F3.wireOp",EDGE,"E54.MirrorCS");var subQ1=sQuery(id+"F3.wireOp",EDGE,"E11.1");var subQ2=makeQuery(id+"F3.imprint","INTERSECT",VERTEX,{"disambiguationData":[OD(0.0)],"derivedFrom":[subQ1,subQ0]});Q18=makeQuery(id+"F3.imprint","IMPRINT",FACE,{"disambiguationData":[TD([[makeQuery(id+"F3.imprint","IMPRINT",EDGE,{"disambiguationData":[TD([[subQ2,-1.0]])],"derivedFrom":subQ1}),-1.0]])]});}
            var Q19;
            {var subQ6=sQuery(id+"F3.wireOp",EDGE,"E55.MirrorCS");Q19=makeQuery(id+"F3.imprint","IMPRINT",FACE,{"disambiguationData":[TD([[makeQuery(id+"F3.imprint","IMPRINT",EDGE,{"derivedFrom":subQ6}),-1.0]])]});}
            var Q20;
            {var subQ0=sQuery(id+"F3.wireOp",EDGE,"E34");var subQ1=sQuery(id+"F3.wireOp",EDGE,"E15");var subQ2=makeQuery(id+"F3.imprint","INTERSECT",VERTEX,{"derivedFrom":[subQ1,subQ0]});Q20=makeQuery(id+"F3.imprint","IMPRINT",FACE,{"disambiguationData":[TD([[makeQuery(id+"F3.imprint","IMPRINT",EDGE,{"disambiguationData":[TD([[subQ2,-1.0]])],"derivedFrom":subQ1}),1.0]])]});}
            var Q21;
            {var subQ5=sQuery(id+"F3.wireOp",EDGE,"E35");Q21=makeQuery(id+"F3.imprint","IMPRINT",FACE,{"disambiguationData":[TD([[makeQuery(id+"F3.imprint","IMPRINT",EDGE,{"derivedFrom":subQ5}),1.0]])]});}
            var Q22;
            {var subQ0=sQuery(id+"F3.wireOp",EDGE,"E32");var subQ1=sQuery(id+"F3.wireOp",EDGE,"E12.MirrorCS");var subQ2=makeQuery(id+"F3.imprint","INTERSECT",VERTEX,{"derivedFrom":[subQ1,subQ0]});Q22=makeQuery(id+"F3.imprint","IMPRINT",FACE,{"disambiguationData":[TD([[makeQuery(id+"F3.imprint","IMPRINT",EDGE,{"disambiguationData":[TD([[subQ2,-1.0]])],"derivedFrom":subQ1}),1.0]])]});}
            var Q23;
            {var subQ0=sQuery(id+"F3.wireOp",EDGE,"E33");Q23=makeQuery(id+"F3.imprint","IMPRINT",FACE,{"disambiguationData":[TD([[makeQuery(id+"F3.imprint","IMPRINT",EDGE,{"derivedFrom":subQ0}),1.0]])]});}
            extrude(context, id + "F5", {"entities" : qUnion([Q0, Q1, Q2, Q3, Q4, Q5, Q6, Q7, Q8, Q9, Q10, Q11, Q12, Q13, Q14, Q15, Q16, Q17, Q18, Q19, Q20, Q21, Q22, Q23]), "operationType" : NewBodyOperationType.REMOVE, "depth" : 5 * mm, "hasSecondDirection" : true, "secondDirectionOppositeDirection" : false, "secondDirectionDepth" : 1 * mm});
        }
    });
